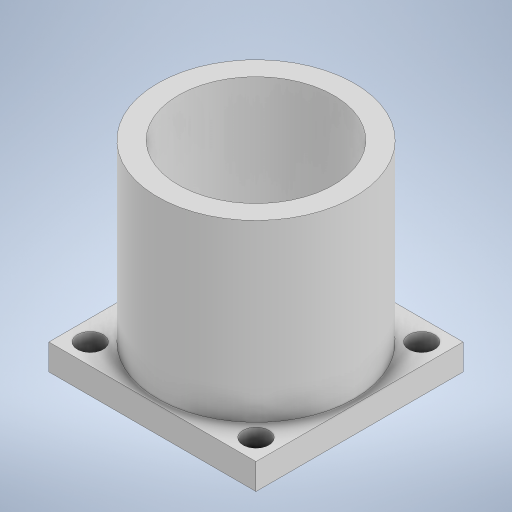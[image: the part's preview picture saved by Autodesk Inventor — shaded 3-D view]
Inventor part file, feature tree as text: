
AUTODESK INVENTOR PART (.ipt)
format: ipt  version: 2023 (Build 270158000, 158)  size: 239,104 bytes
history: native  units: in
note: dims shown in document units (in); Inventor stores cm internally (conversion verified against a paired STEP export)
features: extrude x3, sketch x1
ambient origin geometry x8: Origin, YZ Plane, XZ Plane, XY Plane, X Axis, Y Axis, Z Axis, Center Point
bodies: Solid1 (feature_tree)
feature tree (4):
  sketch  "Sketch1"  dims[d6=1.938in d7=0.0in d10=2.0in d11=2.0in d12=0.25in d13=0.0in d20=0.25in d23=0.25in d24=0.0in]
  extrude  "Extrusion1"  Depth=2.0in
  extrude  "Extrusion3"  Depth=2.0in
  extrude  "Extrusion5"  Depth=0.25in TaperAngle=0.0deg
